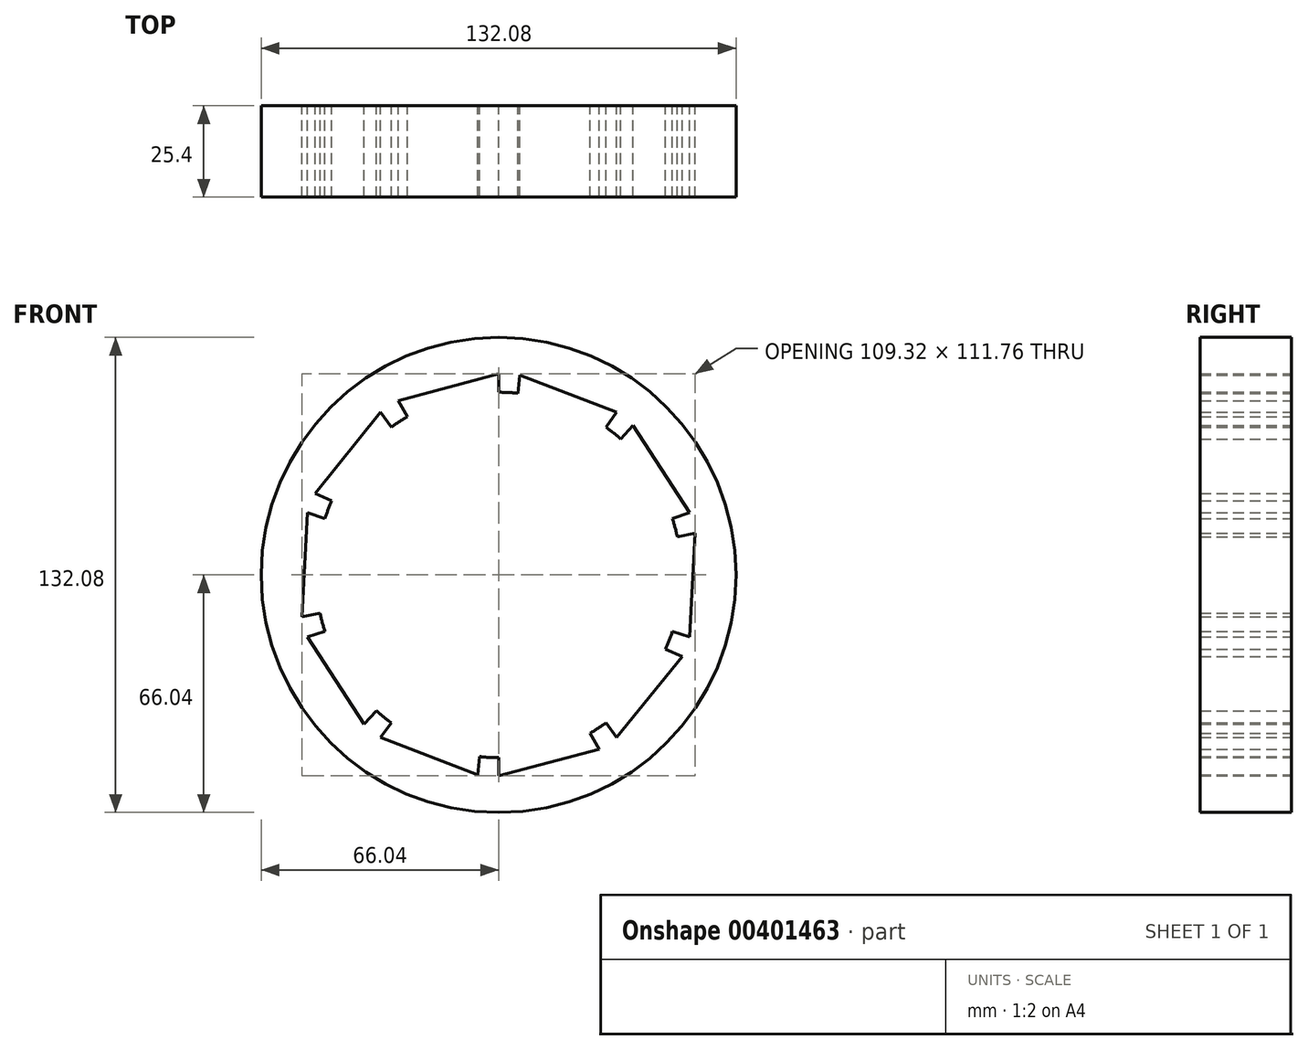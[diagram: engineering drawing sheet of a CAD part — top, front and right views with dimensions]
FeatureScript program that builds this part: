
annotation { "Feature Type Name" : "Feature", "Feature Type Description" : "" }
export const myFeature = defineFeature(function(context is Context, id is Id, definition is map)
    precondition{}
    {
        {
            var Q0;
            Q0=qCreatedBy(makeId("Front.planeOp"),FACE);
            var sketch = newSketch(context, id + "F0", { "sketchPlane" : qUnion([Q0])});
            skCircle(sketch, "E0", {"center": v(0, 0) * mm, "radius": 50.8 * mm});
            skCircle(sketch, "E1", {"center": v(0, 0) * mm, "radius": 55.88 * mm});
            skLineSegment(sketch, "E2", {"start": v(53.98, 14.46) * mm, "end": v(0, 0) * mm});
            skLineSegment(sketch, "E3", {"start": v(0, 0) * mm, "end": v(52.17, -20.03) * mm});
            skLineSegment(sketch, "E4", {"start": v(0, 0) * mm, "end": v(30.43, -46.86) * mm});
            skLineSegment(sketch, "E5", {"start": v(0, 0) * mm, "end": v(-2.92, -55.8) * mm});
            skLineSegment(sketch, "E6", {"start": v(0, 0) * mm, "end": v(-35.17, -43.43) * mm});
            skLineSegment(sketch, "E7", {"start": v(0, 0) * mm, "end": v(-53.98, -14.46) * mm});
            skLineSegment(sketch, "E8", {"start": v(0, 0) * mm, "end": v(-52.17, 20.03) * mm});
            skLineSegment(sketch, "E9", {"start": v(0, 0) * mm, "end": v(-30.43, 46.86) * mm});
            skLineSegment(sketch, "E10", {"start": v(0, 0) * mm, "end": v(2.92, 55.8) * mm});
            skLineSegment(sketch, "E11", {"start": v(0, 0) * mm, "end": v(35.17, 43.43) * mm});
            skLineSegment(sketch, "E12", {"start": v(0, 0) * mm, "end": v(-32.85, 45.2) * mm});
            skLineSegment(sketch, "E13", {"start": v(0, 0) * mm, "end": v(-27.94, 48.4) * mm});
            skLineSegment(sketch, "E14", {"start": v(0, 0) * mm, "end": v(0, 55.88) * mm});
            skLineSegment(sketch, "E15", {"start": v(5.84, 55.57) * mm, "end": v(0, 0) * mm});
            skLineSegment(sketch, "E16", {"start": v(32.85, 45.2) * mm, "end": v(0, 0) * mm});
            skLineSegment(sketch, "E17", {"start": v(0, 0) * mm, "end": v(37.4, 41.53) * mm});
            skLineSegment(sketch, "E18", {"start": v(0, 0) * mm, "end": v(53.15, 17.27) * mm});
            skPoint(sketch, "E19.endSnap0", {"position": v(-26.08, 10.01) * mm});
            skLineSegment(sketch, "E20", {"start": v(0, 0) * mm, "end": v(53.15, -17.27) * mm});
            skLineSegment(sketch, "E21", {"start": v(0, 0) * mm, "end": v(51.05, -22.73) * mm});
            skLineSegment(sketch, "E22", {"start": v(0, 0) * mm, "end": v(54.66, 11.62) * mm});
            skLineSegment(sketch, "E23", {"start": v(0, 0) * mm, "end": v(32.85, -45.2) * mm});
            skLineSegment(sketch, "E24", {"start": v(0, 0) * mm, "end": v(27.94, -48.4) * mm});
            skLineSegment(sketch, "E25", {"start": v(0, 0) * mm, "end": v(-5.84, -55.57) * mm});
            skLineSegment(sketch, "E26", {"start": v(0, 0) * mm, "end": v(0, -55.88) * mm});
            skLineSegment(sketch, "E27", {"start": v(0, 0) * mm, "end": v(-32.85, -45.2) * mm});
            skLineSegment(sketch, "E28", {"start": v(0, 0) * mm, "end": v(-37.4, -41.53) * mm});
            skLineSegment(sketch, "E29", {"start": v(0, 0) * mm, "end": v(-53.15, -17.27) * mm});
            skLineSegment(sketch, "E30", {"start": v(0, 0) * mm, "end": v(-54.66, -11.62) * mm});
            skLineSegment(sketch, "E31", {"start": v(0, 0) * mm, "end": v(-51.05, 22.73) * mm});
            skLineSegment(sketch, "E32", {"start": v(0, 0) * mm, "end": v(-53.15, 17.27) * mm});
            skCircle(sketch, "E33", {"center": v(0, 0) * mm, "radius": 66.04 * mm});
            skLineSegment(sketch, "E34", {"start": v(-32.85, -45.2) * mm, "end": v(-5.84, -55.57) * mm});
            skLineSegment(sketch, "E35", {"start": v(0, -55.88) * mm, "end": v(27.94, -48.4) * mm});
            skLineSegment(sketch, "E36", {"start": v(32.85, -45.2) * mm, "end": v(51.05, -22.73) * mm});
            skLineSegment(sketch, "E37", {"start": v(53.15, -17.27) * mm, "end": v(54.66, 11.62) * mm});
            skLineSegment(sketch, "E38", {"start": v(53.15, 17.27) * mm, "end": v(37.4, 41.53) * mm});
            skLineSegment(sketch, "E39", {"start": v(32.85, 45.2) * mm, "end": v(5.84, 55.57) * mm});
            skLineSegment(sketch, "E40", {"start": v(0, 55.88) * mm, "end": v(-27.94, 48.4) * mm});
            skLineSegment(sketch, "E41", {"start": v(-32.85, 45.2) * mm, "end": v(-51.05, 22.73) * mm});
            skLineSegment(sketch, "E42", {"start": v(-53.15, 17.27) * mm, "end": v(-54.66, -11.62) * mm});
            skLineSegment(sketch, "E43", {"start": v(-53.15, -17.27) * mm, "end": v(-37.4, -41.53) * mm});
            skSolve(sketch);
        }
        {
            var Q0;
            Q0=makeQuery(id+"F0.imprint","IMPRINT",FACE,{"disambiguationData":[TD([[makeQuery(id+"F0.imprint","IMPRINT",EDGE,{"derivedFrom":sQuery(id+"F0.wireOp",EDGE,"E33")}),1.0]])]});
            var Q1;
            {var subQ0=sQuery(id+"F0.wireOp",EDGE,"E31");var subQ1=sQuery(id+"F0.wireOp",EDGE,"E0");var subQ2=makeQuery(id+"F0.imprint","INTERSECT",VERTEX,{"derivedFrom":[subQ1,subQ0]});Q1=makeQuery(id+"F0.imprint","IMPRINT",FACE,{"disambiguationData":[TD([[makeQuery(id+"F0.imprint","IMPRINT",EDGE,{"disambiguationData":[TD([[subQ2,-1.0]])],"derivedFrom":subQ1}),-1.0]])]});}
            var Q2;
            {var subQ0=sQuery(id+"F0.wireOp",EDGE,"E8");var subQ1=sQuery(id+"F0.wireOp",EDGE,"E0");var subQ2=makeQuery(id+"F0.imprint","INTERSECT",VERTEX,{"derivedFrom":[subQ1,subQ0]});Q2=makeQuery(id+"F0.imprint","IMPRINT",FACE,{"disambiguationData":[TD([[makeQuery(id+"F0.imprint","IMPRINT",EDGE,{"disambiguationData":[TD([[subQ2,-1.0]])],"derivedFrom":subQ1}),-1.0]])]});}
            var Q3;
            {var subQ0=sQuery(id+"F0.wireOp",EDGE,"E13");var subQ1=sQuery(id+"F0.wireOp",EDGE,"E0");var subQ2=makeQuery(id+"F0.imprint","INTERSECT",VERTEX,{"derivedFrom":[subQ1,subQ0]});Q3=makeQuery(id+"F0.imprint","IMPRINT",FACE,{"disambiguationData":[TD([[makeQuery(id+"F0.imprint","IMPRINT",EDGE,{"disambiguationData":[TD([[subQ2,-1.0]])],"derivedFrom":subQ1}),-1.0]])]});}
            var Q4;
            {var subQ0=sQuery(id+"F0.wireOp",EDGE,"E9");var subQ1=sQuery(id+"F0.wireOp",EDGE,"E0");var subQ2=makeQuery(id+"F0.imprint","INTERSECT",VERTEX,{"derivedFrom":[subQ1,subQ0]});Q4=makeQuery(id+"F0.imprint","IMPRINT",FACE,{"disambiguationData":[TD([[makeQuery(id+"F0.imprint","IMPRINT",EDGE,{"disambiguationData":[TD([[subQ2,-1.0]])],"derivedFrom":subQ1}),-1.0]])]});}
            var Q5;
            {var subQ0=sQuery(id+"F0.wireOp",EDGE,"E15");var subQ1=sQuery(id+"F0.wireOp",EDGE,"E0");var subQ2=makeQuery(id+"F0.imprint","INTERSECT",VERTEX,{"derivedFrom":[subQ1,subQ0]});Q5=makeQuery(id+"F0.imprint","IMPRINT",FACE,{"disambiguationData":[TD([[makeQuery(id+"F0.imprint","IMPRINT",EDGE,{"disambiguationData":[TD([[subQ2,-1.0]])],"derivedFrom":subQ1}),-1.0]])]});}
            var Q6;
            {var subQ0=sQuery(id+"F0.wireOp",EDGE,"E10");var subQ1=sQuery(id+"F0.wireOp",EDGE,"E0");var subQ2=makeQuery(id+"F0.imprint","INTERSECT",VERTEX,{"derivedFrom":[subQ1,subQ0]});Q6=makeQuery(id+"F0.imprint","IMPRINT",FACE,{"disambiguationData":[TD([[makeQuery(id+"F0.imprint","IMPRINT",EDGE,{"disambiguationData":[TD([[subQ2,-1.0]])],"derivedFrom":subQ1}),-1.0]])]});}
            var Q7;
            {var subQ0=sQuery(id+"F0.wireOp",EDGE,"E11");var subQ1=sQuery(id+"F0.wireOp",EDGE,"E0");var subQ2=makeQuery(id+"F0.imprint","INTERSECT",VERTEX,{"derivedFrom":[subQ1,subQ0]});Q7=makeQuery(id+"F0.imprint","IMPRINT",FACE,{"disambiguationData":[TD([[makeQuery(id+"F0.imprint","IMPRINT",EDGE,{"disambiguationData":[TD([[subQ2,-1.0]])],"derivedFrom":subQ1}),-1.0]])]});}
            var Q8;
            {var subQ0=sQuery(id+"F0.wireOp",EDGE,"E17");var subQ1=sQuery(id+"F0.wireOp",EDGE,"E0");var subQ2=makeQuery(id+"F0.imprint","INTERSECT",VERTEX,{"derivedFrom":[subQ1,subQ0]});Q8=makeQuery(id+"F0.imprint","IMPRINT",FACE,{"disambiguationData":[TD([[makeQuery(id+"F0.imprint","IMPRINT",EDGE,{"disambiguationData":[TD([[subQ2,-1.0]])],"derivedFrom":subQ1}),-1.0]])]});}
            var Q9;
            {var subQ0=sQuery(id+"F0.wireOp",EDGE,"E2");var subQ1=sQuery(id+"F0.wireOp",EDGE,"E0");var subQ2=makeQuery(id+"F0.imprint","INTERSECT",VERTEX,{"derivedFrom":[subQ1,subQ0]});Q9=makeQuery(id+"F0.imprint","IMPRINT",FACE,{"disambiguationData":[TD([[makeQuery(id+"F0.imprint","IMPRINT",EDGE,{"disambiguationData":[TD([[subQ2,-1.0]])],"derivedFrom":subQ1}),-1.0]])]});}
            var Q10;
            {var subQ0=sQuery(id+"F0.wireOp",EDGE,"E2");var subQ1=sQuery(id+"F0.wireOp",EDGE,"E0");var subQ2=makeQuery(id+"F0.imprint","INTERSECT",VERTEX,{"derivedFrom":[subQ1,subQ0]});Q10=makeQuery(id+"F0.imprint","IMPRINT",FACE,{"disambiguationData":[TD([[makeQuery(id+"F0.imprint","IMPRINT",EDGE,{"disambiguationData":[TD([[subQ2,1.0]])],"derivedFrom":subQ1}),-1.0]])]});}
            var Q11;
            {var subQ0=sQuery(id+"F0.wireOp",EDGE,"E3");var subQ1=sQuery(id+"F0.wireOp",EDGE,"E0");var subQ2=makeQuery(id+"F0.imprint","INTERSECT",VERTEX,{"derivedFrom":[subQ1,subQ0]});Q11=makeQuery(id+"F0.imprint","IMPRINT",FACE,{"disambiguationData":[TD([[makeQuery(id+"F0.imprint","IMPRINT",EDGE,{"disambiguationData":[TD([[subQ2,-1.0]])],"derivedFrom":subQ1}),-1.0]])]});}
            var Q12;
            {var subQ0=sQuery(id+"F0.wireOp",EDGE,"E21");var subQ1=sQuery(id+"F0.wireOp",EDGE,"E0");var subQ2=makeQuery(id+"F0.imprint","INTERSECT",VERTEX,{"derivedFrom":[subQ1,subQ0]});Q12=makeQuery(id+"F0.imprint","IMPRINT",FACE,{"disambiguationData":[TD([[makeQuery(id+"F0.imprint","IMPRINT",EDGE,{"disambiguationData":[TD([[subQ2,-1.0]])],"derivedFrom":subQ1}),-1.0]])]});}
            var Q13;
            {var subQ0=sQuery(id+"F0.wireOp",EDGE,"E4");var subQ1=sQuery(id+"F0.wireOp",EDGE,"E0");var subQ2=makeQuery(id+"F0.imprint","INTERSECT",VERTEX,{"derivedFrom":[subQ1,subQ0]});Q13=makeQuery(id+"F0.imprint","IMPRINT",FACE,{"disambiguationData":[TD([[makeQuery(id+"F0.imprint","IMPRINT",EDGE,{"disambiguationData":[TD([[subQ2,-1.0]])],"derivedFrom":subQ1}),-1.0]])]});}
            var Q14;
            {var subQ0=sQuery(id+"F0.wireOp",EDGE,"E24");var subQ1=sQuery(id+"F0.wireOp",EDGE,"E0");var subQ2=makeQuery(id+"F0.imprint","INTERSECT",VERTEX,{"derivedFrom":[subQ1,subQ0]});Q14=makeQuery(id+"F0.imprint","IMPRINT",FACE,{"disambiguationData":[TD([[makeQuery(id+"F0.imprint","IMPRINT",EDGE,{"disambiguationData":[TD([[subQ2,-1.0]])],"derivedFrom":subQ1}),-1.0]])]});}
            var Q15;
            {var subQ0=sQuery(id+"F0.wireOp",EDGE,"E5");var subQ1=sQuery(id+"F0.wireOp",EDGE,"E0");var subQ2=makeQuery(id+"F0.imprint","INTERSECT",VERTEX,{"derivedFrom":[subQ1,subQ0]});Q15=makeQuery(id+"F0.imprint","IMPRINT",FACE,{"disambiguationData":[TD([[makeQuery(id+"F0.imprint","IMPRINT",EDGE,{"disambiguationData":[TD([[subQ2,-1.0]])],"derivedFrom":subQ1}),-1.0]])]});}
            var Q16;
            {var subQ0=sQuery(id+"F0.wireOp",EDGE,"E25");var subQ1=sQuery(id+"F0.wireOp",EDGE,"E0");var subQ2=makeQuery(id+"F0.imprint","INTERSECT",VERTEX,{"derivedFrom":[subQ1,subQ0]});Q16=makeQuery(id+"F0.imprint","IMPRINT",FACE,{"disambiguationData":[TD([[makeQuery(id+"F0.imprint","IMPRINT",EDGE,{"disambiguationData":[TD([[subQ2,-1.0]])],"derivedFrom":subQ1}),-1.0]])]});}
            var Q17;
            {var subQ0=sQuery(id+"F0.wireOp",EDGE,"E6");var subQ1=sQuery(id+"F0.wireOp",EDGE,"E0");var subQ2=makeQuery(id+"F0.imprint","INTERSECT",VERTEX,{"derivedFrom":[subQ1,subQ0]});Q17=makeQuery(id+"F0.imprint","IMPRINT",FACE,{"disambiguationData":[TD([[makeQuery(id+"F0.imprint","IMPRINT",EDGE,{"disambiguationData":[TD([[subQ2,-1.0]])],"derivedFrom":subQ1}),-1.0]])]});}
            var Q18;
            {var subQ0=sQuery(id+"F0.wireOp",EDGE,"E28");var subQ1=sQuery(id+"F0.wireOp",EDGE,"E0");var subQ2=makeQuery(id+"F0.imprint","INTERSECT",VERTEX,{"derivedFrom":[subQ1,subQ0]});Q18=makeQuery(id+"F0.imprint","IMPRINT",FACE,{"disambiguationData":[TD([[makeQuery(id+"F0.imprint","IMPRINT",EDGE,{"disambiguationData":[TD([[subQ2,-1.0]])],"derivedFrom":subQ1}),-1.0]])]});}
            var Q19;
            {var subQ0=sQuery(id+"F0.wireOp",EDGE,"E7");var subQ1=sQuery(id+"F0.wireOp",EDGE,"E0");var subQ2=makeQuery(id+"F0.imprint","INTERSECT",VERTEX,{"derivedFrom":[subQ1,subQ0]});Q19=makeQuery(id+"F0.imprint","IMPRINT",FACE,{"disambiguationData":[TD([[makeQuery(id+"F0.imprint","IMPRINT",EDGE,{"disambiguationData":[TD([[subQ2,-1.0]])],"derivedFrom":subQ1}),-1.0]])]});}
            var Q20;
            {var subQ0=sQuery(id+"F0.wireOp",EDGE,"E30");var subQ1=sQuery(id+"F0.wireOp",EDGE,"E0");var subQ2=makeQuery(id+"F0.imprint","INTERSECT",VERTEX,{"derivedFrom":[subQ1,subQ0]});Q20=makeQuery(id+"F0.imprint","IMPRINT",FACE,{"disambiguationData":[TD([[makeQuery(id+"F0.imprint","IMPRINT",EDGE,{"disambiguationData":[TD([[subQ2,-1.0]])],"derivedFrom":subQ1}),-1.0]])]});}
            var Q21;
            {var subQ0=sQuery(id+"F0.wireOp",EDGE,"E43");Q21=makeQuery(id+"F0.imprint","IMPRINT",FACE,{"disambiguationData":[TD([[makeQuery(id+"F0.imprint","IMPRINT",EDGE,{"derivedFrom":subQ0}),-1.0]])]});}
            var Q22;
            {var subQ0=sQuery(id+"F0.wireOp",EDGE,"E42");Q22=makeQuery(id+"F0.imprint","IMPRINT",FACE,{"disambiguationData":[TD([[makeQuery(id+"F0.imprint","IMPRINT",EDGE,{"derivedFrom":subQ0}),-1.0]])]});}
            var Q23;
            {var subQ0=sQuery(id+"F0.wireOp",EDGE,"E41");Q23=makeQuery(id+"F0.imprint","IMPRINT",FACE,{"disambiguationData":[TD([[makeQuery(id+"F0.imprint","IMPRINT",EDGE,{"derivedFrom":subQ0}),-1.0]])]});}
            var Q24;
            {var subQ0=sQuery(id+"F0.wireOp",EDGE,"E40");Q24=makeQuery(id+"F0.imprint","IMPRINT",FACE,{"disambiguationData":[TD([[makeQuery(id+"F0.imprint","IMPRINT",EDGE,{"derivedFrom":subQ0}),-1.0]])]});}
            var Q25;
            {var subQ0=sQuery(id+"F0.wireOp",EDGE,"E39");Q25=makeQuery(id+"F0.imprint","IMPRINT",FACE,{"disambiguationData":[TD([[makeQuery(id+"F0.imprint","IMPRINT",EDGE,{"derivedFrom":subQ0}),-1.0]])]});}
            var Q26;
            {var subQ0=sQuery(id+"F0.wireOp",EDGE,"E38");Q26=makeQuery(id+"F0.imprint","IMPRINT",FACE,{"disambiguationData":[TD([[makeQuery(id+"F0.imprint","IMPRINT",EDGE,{"derivedFrom":subQ0}),-1.0]])]});}
            var Q27;
            {var subQ0=sQuery(id+"F0.wireOp",EDGE,"E37");Q27=makeQuery(id+"F0.imprint","IMPRINT",FACE,{"disambiguationData":[TD([[makeQuery(id+"F0.imprint","IMPRINT",EDGE,{"derivedFrom":subQ0}),-1.0]])]});}
            var Q28;
            {var subQ0=sQuery(id+"F0.wireOp",EDGE,"E36");Q28=makeQuery(id+"F0.imprint","IMPRINT",FACE,{"disambiguationData":[TD([[makeQuery(id+"F0.imprint","IMPRINT",EDGE,{"derivedFrom":subQ0}),-1.0]])]});}
            var Q29;
            {var subQ0=sQuery(id+"F0.wireOp",EDGE,"E35");Q29=makeQuery(id+"F0.imprint","IMPRINT",FACE,{"disambiguationData":[TD([[makeQuery(id+"F0.imprint","IMPRINT",EDGE,{"derivedFrom":subQ0}),-1.0]])]});}
            var Q30;
            {var subQ0=sQuery(id+"F0.wireOp",EDGE,"E34");Q30=makeQuery(id+"F0.imprint","IMPRINT",FACE,{"disambiguationData":[TD([[makeQuery(id+"F0.imprint","IMPRINT",EDGE,{"derivedFrom":subQ0}),-1.0]])]});}
            extrude(context, id + "F1", {"entities" : qUnion([Q0, Q1, Q2, Q3, Q4, Q5, Q6, Q7, Q8, Q9, Q10, Q11, Q12, Q13, Q14, Q15, Q16, Q17, Q18, Q19, Q20, Q21, Q22, Q23, Q24, Q25, Q26, Q27, Q28, Q29, Q30]), "depth" : 25.4 * mm});
        }
    });
